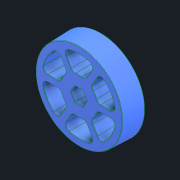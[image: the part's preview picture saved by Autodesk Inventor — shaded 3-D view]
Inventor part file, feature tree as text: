
AUTODESK INVENTOR PART (.ipt)
format: ipt  version: 2021 (Build 250183000, 183)  size: 742,400 bytes
history: native  units: in
note: dims shown in document units (in); Inventor stores cm internally (conversion verified against a paired STEP export)
features: fillet x1
ambient origin geometry x8: Origin, YZ Plane, XZ Plane, XY Plane, X Axis, Y Axis, Z Axis, Center Point
bodies: Solid1 (feature_tree)
feature tree (1):
  fillet  "Fillet3"  [1 undecoded]
note: 1 required parameter value undecoded (feature->parameter linkage not recoverable at this tier; creation-order binding heuristic only, values carry confidence <= 0.55)
